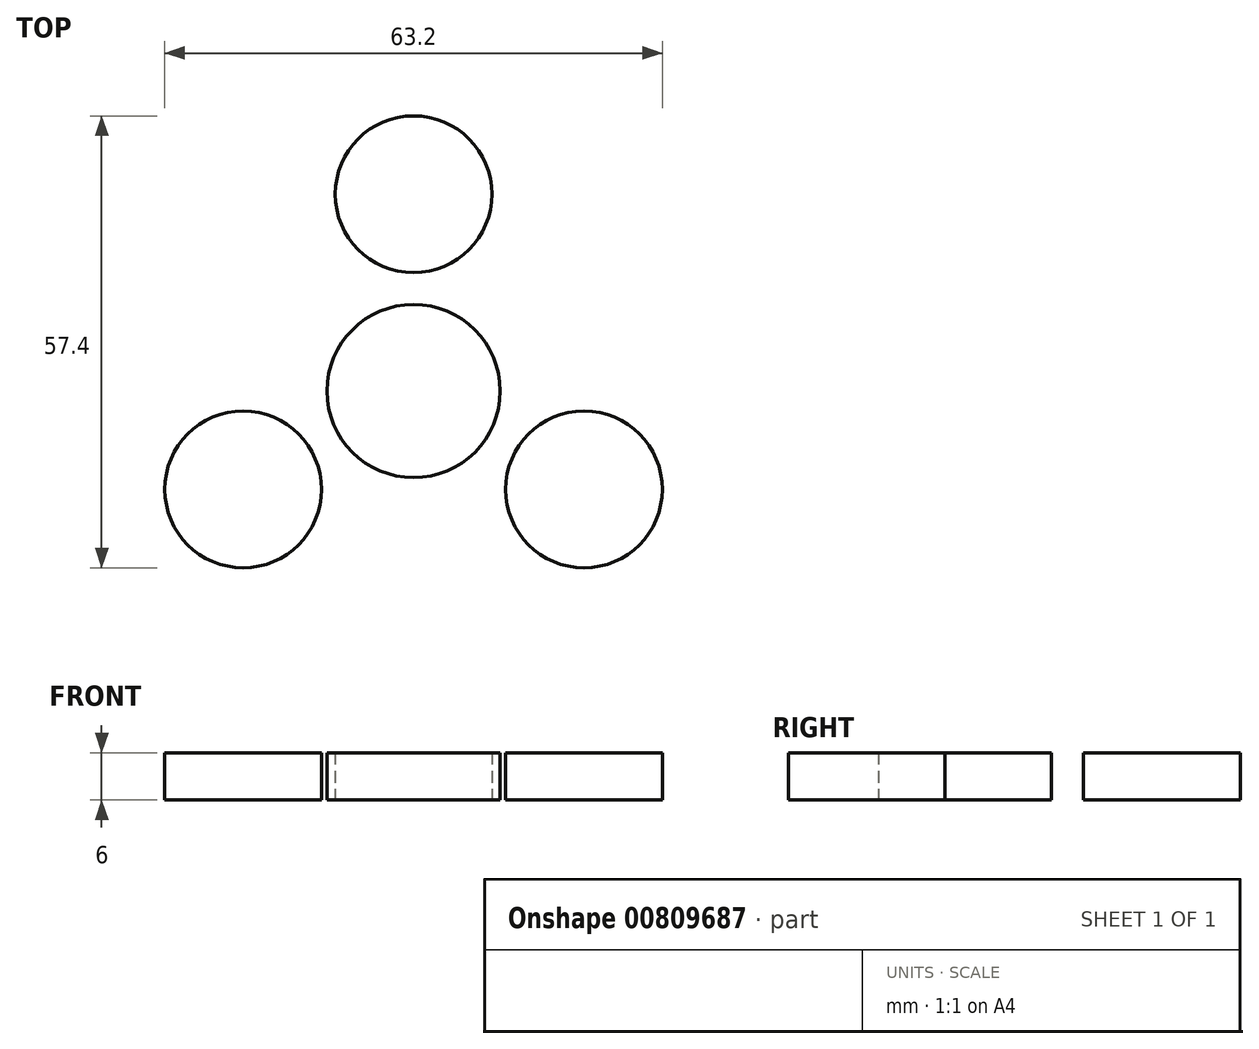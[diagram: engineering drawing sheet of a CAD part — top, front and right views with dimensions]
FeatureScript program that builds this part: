
annotation { "Feature Type Name" : "Feature", "Feature Type Description" : "" }
export const myFeature = defineFeature(function(context is Context, id is Id, definition is map)
    precondition{}
    {
        {
            var Q0;
            Q0=qCreatedBy(makeId("Top.planeOp"),FACE);
            var sketch = newSketch(context, id + "F0", { "sketchPlane" : qUnion([Q0])});
            skArc(sketch, "E0", {"start": v(9.53, 5.5) * mm, "mid": v(0, 11) * mm, "end": v(-9.53, 5.5) * mm});
            skCircle(sketch, "E1", {"center": v(0, 25) * mm, "radius": 9.95 * mm});
            skArc(sketch, "E2", {"start": v(-8.3, 12.5) * mm, "mid": v(-10.93, 10.27) * mm, "end": v(-13, 7.5) * mm});
            skArc(sketch, "E3", {"start": v(8.3, 12.5) * mm, "mid": v(0, 40) * mm, "end": v(-8.3, 12.5) * mm});
            skArc(sketch, "E4.trimOffspring", {"start": v(13, 7.5) * mm, "mid": v(10.93, 10.27) * mm, "end": v(8.3, 12.5) * mm});
            skArc(sketch, "E5.1.0", {"start": v(-14.97, 0.93) * mm, "mid": v(-34.64, -20) * mm, "end": v(-6.68, -13.43) * mm});
            skCircle(sketch, "E5.1.1", {"center": v(-21.65, -12.5) * mm, "radius": 9.95 * mm});
            skArc(sketch, "E5.1.2", {"start": v(-9.53, 5.5) * mm, "mid": v(-9.53, -5.5) * mm, "end": v(0, -11) * mm});
            skArc(sketch, "E5.2.0", {"start": v(6.68, -13.43) * mm, "mid": v(34.64, -20) * mm, "end": v(14.97, 0.93) * mm});
            skCircle(sketch, "E5.2.1", {"center": v(21.65, -12.5) * mm, "radius": 9.95 * mm});
            skArc(sketch, "E5.2.2", {"start": v(0, -11) * mm, "mid": v(9.53, -5.5) * mm, "end": v(9.53, 5.5) * mm});
            skSolve(sketch);
        }
        {
            var Q0;
            Q0 = qSketchRegion(id + "F0", true);
            extrude(context, id + "F1", {"entities" : qUnion([Q0]), "depth" : 6 * mm, "offsetDistance" : 25 * mm});
        }
    });
